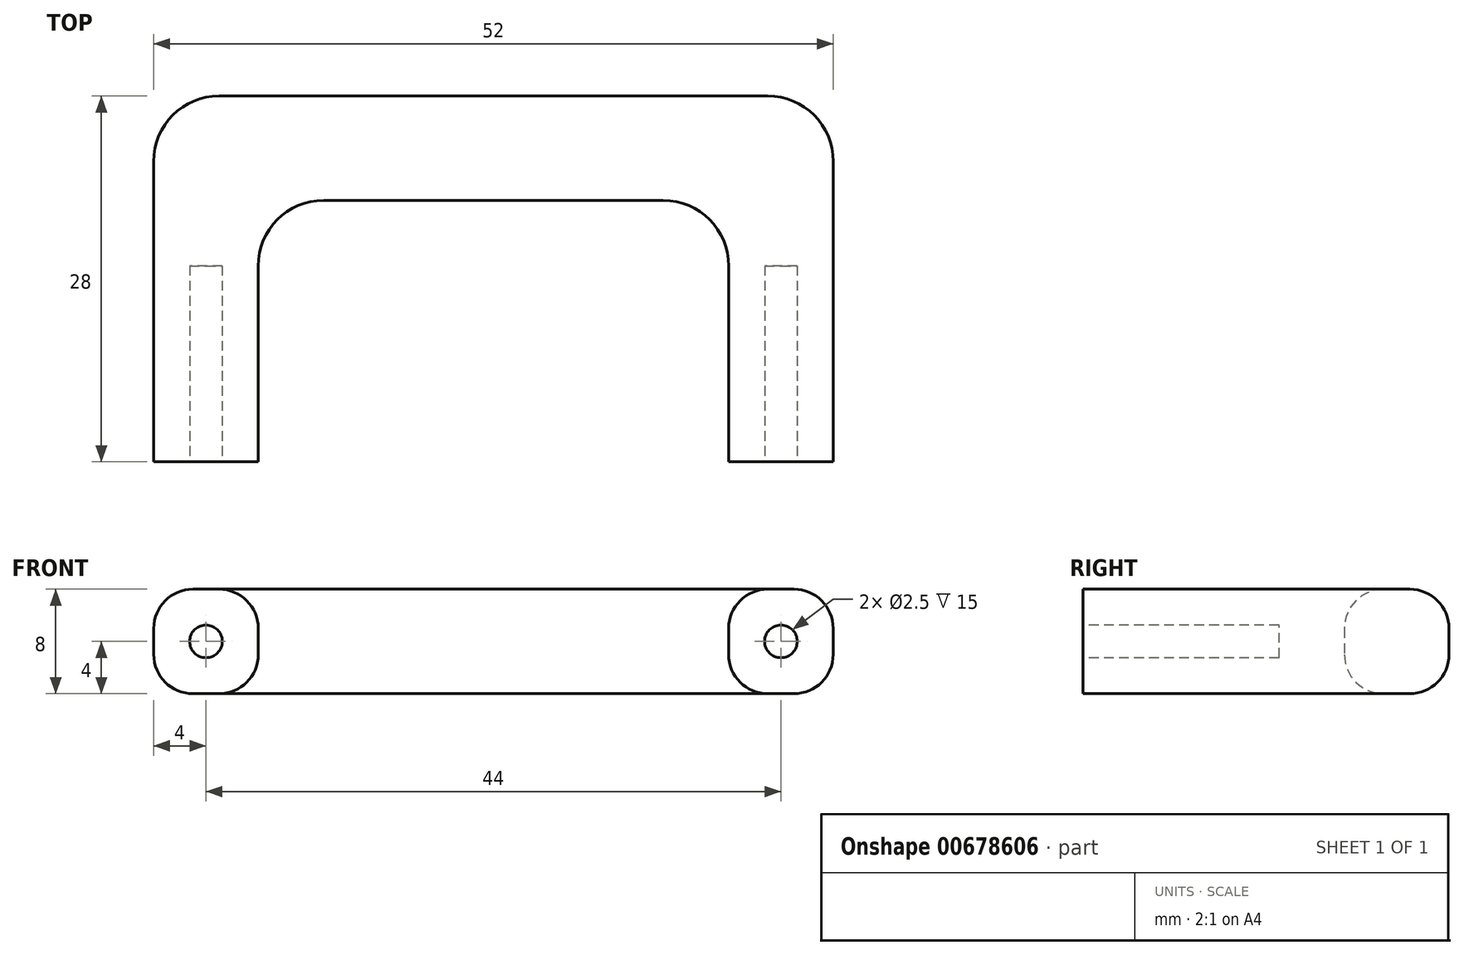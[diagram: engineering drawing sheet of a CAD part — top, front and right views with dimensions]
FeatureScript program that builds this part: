
annotation { "Feature Type Name" : "Feature", "Feature Type Description" : "" }
export const myFeature = defineFeature(function(context is Context, id is Id, definition is map)
    precondition{}
    {
        {
            var Q0;
            Q0=qCreatedBy(makeId("Top.planeOp"),FACE);
            var sketch = newSketch(context, id + "F0", { "sketchPlane" : qUnion([Q0])});
            skLineSegment(sketch, "E0.bottom", {"start": v(-8, -30.98) * mm, "end": v(44, -30.98) * mm});
            skLineSegment(sketch, "E0.top", {"start": v(-8, -58.98) * mm, "end": v(0, -58.98) * mm});
            skLineSegment(sketch, "E0.left", {"start": v(-8, -30.98) * mm, "end": v(-8, -58.98) * mm});
            skLineSegment(sketch, "E0.right", {"start": v(44, -30.98) * mm, "end": v(44, -58.98) * mm});
            skLineSegment(sketch, "E1.bottom", {"start": v(0, -38.98) * mm, "end": v(36, -38.98) * mm});
            skLineSegment(sketch, "E1.left", {"start": v(0, -38.98) * mm, "end": v(0, -58.98) * mm});
            skLineSegment(sketch, "E1.right", {"start": v(36, -38.98) * mm, "end": v(36, -58.98) * mm});
            skLineSegment(sketch, "E2.trimOffspring", {"start": v(36, -58.98) * mm, "end": v(44, -58.98) * mm});
            skSolve(sketch);
        }
        {
            var Q0;
            Q0 = qSketchRegion(id + "F0", true);
            extrude(context, id + "F1", {"entities" : qUnion([Q0]), "depth" : 8 * mm, "offsetDistance" : 25 * mm});
        }
        {
            var Q0;
            Q0=makeQuery(id+"F1.opExtrude","SWEPT_EDGE",EDGE,{"disambiguationData":[OSD([sQuery(id+"F0.wireOp",EDGE,"E0.bottom"),sQuery(id+"F0.wireOp",EDGE,"E0.left")])]});
            var Q1;
            Q1=makeQuery(id+"F1.opExtrude","SWEPT_EDGE",EDGE,{"disambiguationData":[OSD([sQuery(id+"F0.wireOp",EDGE,"E0.bottom"),sQuery(id+"F0.wireOp",EDGE,"E0.right")])]});
            var Q2;
            Q2=makeQuery(id+"F1.opExtrude","SWEPT_EDGE",EDGE,{"disambiguationData":[OSD([sQuery(id+"F0.wireOp",EDGE,"E1.bottom"),sQuery(id+"F0.wireOp",EDGE,"E1.left")])]});
            var Q3;
            Q3=makeQuery(id+"F1.opExtrude","SWEPT_EDGE",EDGE,{"disambiguationData":[OSD([sQuery(id+"F0.wireOp",EDGE,"E1.bottom"),sQuery(id+"F0.wireOp",EDGE,"E1.right")])]});
            fillet(context, id + "F2", {"entities" : qUnion([Q0, Q1, Q2, Q3]), "radius" : 5 * mm, "tangentPropagation" : true, "allowEdgeOverflow" : false});
        }
        {
            var Q0;
            Q0=makeQuery(id+"F1.opExtrude","CAP_EDGE",EDGE,{"disambiguationData":[OSD([sQuery(id+"F0.wireOp",EDGE,"E1.bottom")])],"isStart":false});
            var Q1;
            Q1=makeQuery(id+"F1.opExtrude","CAP_EDGE",EDGE,{"disambiguationData":[OSD([sQuery(id+"F0.wireOp",EDGE,"E0.right")])],"isStart":false});
            var Q2;
            Q2=makeQuery(id+"F1.opExtrude","CAP_EDGE",EDGE,{"disambiguationData":[OSD([sQuery(id+"F0.wireOp",EDGE,"E0.right")])],"isStart":true});
            var Q3;
            Q3=makeQuery(id+"F1.opExtrude","CAP_EDGE",EDGE,{"disambiguationData":[OSD([sQuery(id+"F0.wireOp",EDGE,"E1.right")])],"isStart":true});
            fillet(context, id + "F3", {"entities" : qUnion([Q0, Q1, Q2, Q3]), "radius" : 3 * mm, "tangentPropagation" : true, "allowEdgeOverflow" : false});
        }
        {
            var Q0;
            Q0=makeQuery(id+"F1.opExtrude","SWEPT_FACE",FACE,{"disambiguationData":[OSD([sQuery(id+"F0.wireOp",EDGE,"E2.trimOffspring")])]});
            var sketch = newSketch(context, id + "F4", { "sketchPlane" : qUnion([Q0])});
            skCircle(sketch, "E3", {"center": v(-4, 4) * mm, "radius": 1.25 * mm});
            skCircle(sketch, "E4", {"center": v(40, 4) * mm, "radius": 1.25 * mm});
            skSolve(sketch);
        }
        {
            var Q0;
            Q0=makeQuery(id+"F4.imprint","IMPRINT",FACE,{"disambiguationData":[TD([[makeQuery(id+"F4.imprint","IMPRINT",EDGE,{"derivedFrom":sQuery(id+"F4.wireOp",EDGE,"E4")}),1.0]])]});
            var Q1;
            Q1=makeQuery(id+"F4.imprint","IMPRINT",FACE,{"disambiguationData":[TD([[makeQuery(id+"F4.imprint","IMPRINT",EDGE,{"derivedFrom":sQuery(id+"F4.wireOp",EDGE,"E3")}),1.0]])]});
            extrude(context, id + "F5", {"entities" : qUnion([Q0, Q1]), "operationType" : NewBodyOperationType.REMOVE, "oppositeDirection" : true, "depth" : 15 * mm, "offsetDistance" : 25 * mm});
        }
    });
